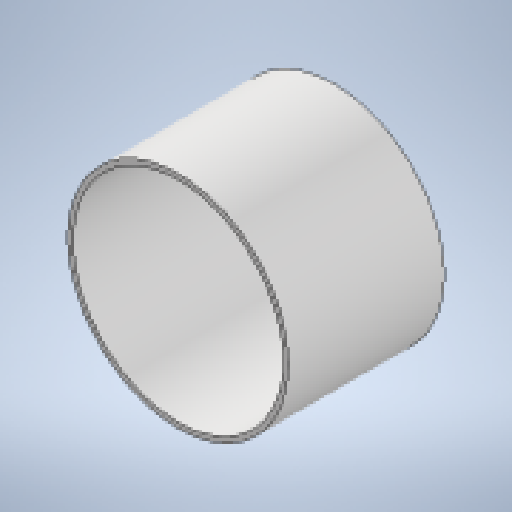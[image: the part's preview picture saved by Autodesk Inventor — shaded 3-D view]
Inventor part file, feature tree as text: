
AUTODESK INVENTOR PART (.ipt)
format: ipt  version: 2025 (Build 290162010, 162A)  size: 146,944 bytes
history: native  units: mm
features: extrude x1, sketch x1
ambient origin geometry x8: Origin, YZ Plane, XZ Plane, XY Plane, X Axis, Y Axis, Z Axis, Center Point
bodies: Solid1 (feature_tree)
feature tree (2):
  extrude  "Extrusion1"  Depth=250.0mm
  sketch  "Sketch1"  dims[d0=170.0mm d1=4.0mm d2=250.0mm d3=0.0mm]
